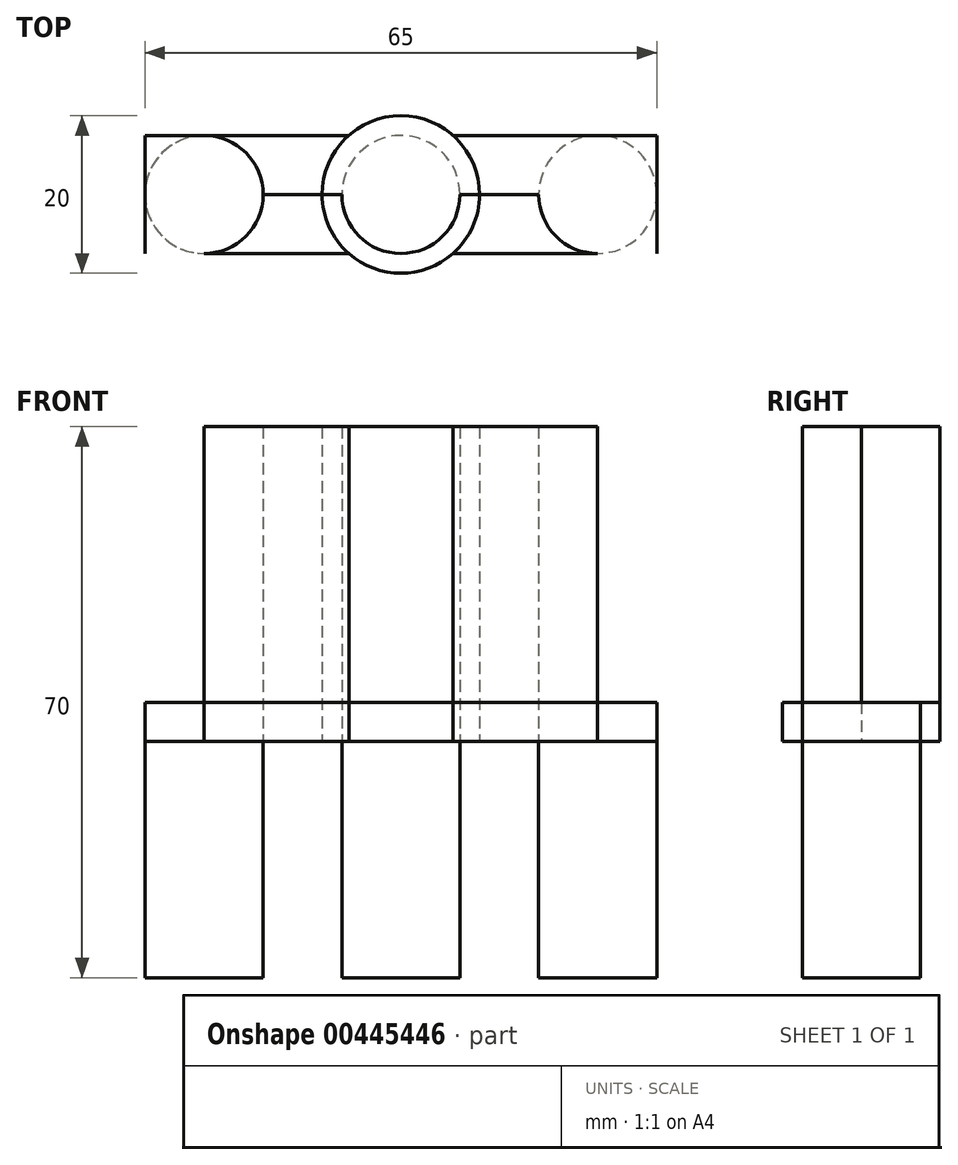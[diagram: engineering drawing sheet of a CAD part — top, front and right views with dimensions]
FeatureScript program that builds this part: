
annotation { "Feature Type Name" : "Feature", "Feature Type Description" : "" }
export const myFeature = defineFeature(function(context is Context, id is Id, definition is map)
    precondition{}
    {
        {
            var Q0;
            Q0=qCreatedBy(makeId("Top.planeOp"),FACE);
            var sketch = newSketch(context, id + "F0", { "sketchPlane" : qUnion([Q0])});
            skLineSegment(sketch, "E0.bottom", {"start": v(32.5, -7.5) * mm, "end": v(-32.5, -7.5) * mm});
            skLineSegment(sketch, "E0.top", {"start": v(32.5, 7.5) * mm, "end": v(-32.5, 7.5) * mm});
            skLineSegment(sketch, "E0.left", {"start": v(32.5, -7.5) * mm, "end": v(32.5, 7.5) * mm});
            skLineSegment(sketch, "E0.right", {"start": v(-32.5, -7.5) * mm, "end": v(-32.5, 7.5) * mm});
            skPoint(sketch, "E0.middle", {"position": v(0, 0) * mm});
            skCircle(sketch, "E1", {"center": v(0, 0) * mm, "radius": 10 * mm});
            skCircle(sketch, "E2", {"center": v(0, 0) * mm, "radius": 7.5 * mm});
            skLineSegment(sketch, "E3", {"start": v(0, 0) * mm, "end": v(25, 0) * mm});
            skLineSegment(sketch, "E4", {"start": v(0, 0) * mm, "end": v(-25, 0) * mm});
            skCircle(sketch, "E5", {"center": v(-25, 0) * mm, "radius": 7.5 * mm});
            skCircle(sketch, "E6", {"center": v(25, 0) * mm, "radius": 7.5 * mm});
            skSolve(sketch);
        }
        {
            var Q0;
            Q0 = qSketchRegion(id + "F0", true);
            var Q1;
            {var subQ0=sQuery(id+"F0.wireOp",EDGE,"E2");var subQ1=makeQuery(id+"F0.imprint","INTERSECT",VERTEX,{"derivedFrom":[sQuery(id+"F0.wireOp",EDGE,"E0.top"),subQ0]});Q1=makeQuery(id+"F0.imprint","IMPRINT",FACE,{"disambiguationData":[TD([[makeQuery(id+"F0.imprint","IMPRINT",EDGE,{"disambiguationData":[TD([[subQ1,1.0]])],"derivedFrom":subQ0}),1.0]])]});}
            var Q2;
            {var subQ0=sQuery(id+"F0.wireOp",EDGE,"E2");var subQ1=makeQuery(id+"F0.imprint","INTERSECT",VERTEX,{"derivedFrom":[sQuery(id+"F0.wireOp",EDGE,"E0.bottom"),subQ0]});Q2=makeQuery(id+"F0.imprint","IMPRINT",FACE,{"disambiguationData":[TD([[makeQuery(id+"F0.imprint","IMPRINT",EDGE,{"disambiguationData":[TD([[subQ1,1.0]])],"derivedFrom":subQ0}),1.0]])]});}
            extrude(context, id + "F1", {"entities" : qUnion([Q0, Q1, Q2]), "depth" : 5 * mm});
        }
        {
            var Q0;
            {var subQ0=sQuery(id+"F0.wireOp",EDGE,"E1");var subQ1=sQuery(id+"F0.wireOp",EDGE,"E0.top");var subQ2=makeQuery(id+"F0.imprint","INTERSECT",VERTEX,{"disambiguationData":[OD(0.0)],"derivedFrom":[subQ1,subQ0]});Q0=makeQuery(id+"F0.imprint","IMPRINT",FACE,{"disambiguationData":[TD([[makeQuery(id+"F0.imprint","IMPRINT",EDGE,{"disambiguationData":[TD([[subQ2,-1.0]])],"derivedFrom":subQ1}),-1.0]])]});}
            var Q1;
            {var subQ0=sQuery(id+"F0.wireOp",EDGE,"E1");var subQ1=sQuery(id+"F0.wireOp",EDGE,"E0.top");var subQ2=makeQuery(id+"F0.imprint","INTERSECT",VERTEX,{"disambiguationData":[OD(1.0)],"derivedFrom":[subQ1,subQ0]});Q1=makeQuery(id+"F0.imprint","IMPRINT",FACE,{"disambiguationData":[TD([[makeQuery(id+"F0.imprint","IMPRINT",EDGE,{"disambiguationData":[TD([[subQ2,1.0]])],"derivedFrom":subQ1}),1.0]])]});}
            var Q2;
            {var subQ0=sQuery(id+"F0.wireOp",EDGE,"E2");var subQ1=makeQuery(id+"F0.imprint","INTERSECT",VERTEX,{"derivedFrom":[sQuery(id+"F0.wireOp",EDGE,"E0.top"),subQ0]});Q2=makeQuery(id+"F0.imprint","IMPRINT",FACE,{"disambiguationData":[TD([[makeQuery(id+"F0.imprint","IMPRINT",EDGE,{"disambiguationData":[TD([[subQ1,1.0]])],"derivedFrom":subQ0}),1.0]])]});}
            var Q3;
            {var subQ0=sQuery(id+"F0.wireOp",EDGE,"E1");var subQ1=sQuery(id+"F0.wireOp",EDGE,"E0.top");var subQ2=makeQuery(id+"F0.imprint","INTERSECT",VERTEX,{"disambiguationData":[OD(0.0)],"derivedFrom":[subQ1,subQ0]});Q3=makeQuery(id+"F0.imprint","IMPRINT",FACE,{"disambiguationData":[TD([[makeQuery(id+"F0.imprint","IMPRINT",EDGE,{"disambiguationData":[TD([[subQ2,-1.0]])],"derivedFrom":subQ1}),1.0]])]});}
            var Q4;
            {var subQ0=sQuery(id+"F0.wireOp",EDGE,"E2");var subQ1=makeQuery(id+"F0.imprint","INTERSECT",VERTEX,{"derivedFrom":[sQuery(id+"F0.wireOp",EDGE,"E0.bottom"),subQ0]});Q4=makeQuery(id+"F0.imprint","IMPRINT",FACE,{"disambiguationData":[TD([[makeQuery(id+"F0.imprint","IMPRINT",EDGE,{"disambiguationData":[TD([[subQ1,1.0]])],"derivedFrom":subQ0}),1.0]])]});}
            var Q5;
            {var subQ0=sQuery(id+"F0.wireOp",EDGE,"E1");var subQ1=sQuery(id+"F0.wireOp",EDGE,"E0.bottom");var subQ2=makeQuery(id+"F0.imprint","INTERSECT",VERTEX,{"disambiguationData":[OD(0.0)],"derivedFrom":[subQ1,subQ0]});Q5=makeQuery(id+"F0.imprint","IMPRINT",FACE,{"disambiguationData":[TD([[makeQuery(id+"F0.imprint","IMPRINT",EDGE,{"disambiguationData":[TD([[subQ2,-1.0]])],"derivedFrom":subQ1}),1.0]])]});}
            var Q6;
            {var subQ0=sQuery(id+"F0.wireOp",EDGE,"E1");var subQ1=sQuery(id+"F0.wireOp",EDGE,"E0.bottom");var subQ2=makeQuery(id+"F0.imprint","INTERSECT",VERTEX,{"disambiguationData":[OD(0.0)],"derivedFrom":[subQ1,subQ0]});Q6=makeQuery(id+"F0.imprint","IMPRINT",FACE,{"disambiguationData":[TD([[makeQuery(id+"F0.imprint","IMPRINT",EDGE,{"disambiguationData":[TD([[subQ2,-1.0]])],"derivedFrom":subQ1}),-1.0]])]});}
            var Q7;
            {var subQ0=sQuery(id+"F0.wireOp",EDGE,"E1");var subQ1=sQuery(id+"F0.wireOp",EDGE,"E0.bottom");var subQ2=makeQuery(id+"F0.imprint","INTERSECT",VERTEX,{"disambiguationData":[OD(1.0)],"derivedFrom":[subQ1,subQ0]});Q7=makeQuery(id+"F0.imprint","IMPRINT",FACE,{"disambiguationData":[TD([[makeQuery(id+"F0.imprint","IMPRINT",EDGE,{"disambiguationData":[TD([[subQ2,1.0]])],"derivedFrom":subQ1}),-1.0]])]});}
            extrude(context, id + "F2", {"entities" : qUnion([Q0, Q1, Q2, Q3, Q4, Q5, Q6, Q7]), "depth" : 40 * mm});
        }
        {
            var Q0;
            {var subQ0=sQuery(id+"F0.wireOp",EDGE,"E5");var subQ1=makeQuery(id+"F0.imprint","INTERSECT",VERTEX,{"derivedFrom":[sQuery(id+"F0.wireOp",EDGE,"E0.top"),subQ0]});Q0=makeQuery(id+"F0.imprint","IMPRINT",FACE,{"disambiguationData":[TD([[makeQuery(id+"F0.imprint","IMPRINT",EDGE,{"disambiguationData":[TD([[subQ1,1.0]])],"derivedFrom":subQ0}),1.0]])]});}
            var Q1;
            {var subQ0=sQuery(id+"F0.wireOp",EDGE,"E2");var subQ1=makeQuery(id+"F0.imprint","INTERSECT",VERTEX,{"derivedFrom":[sQuery(id+"F0.wireOp",EDGE,"E0.top"),subQ0]});Q1=makeQuery(id+"F0.imprint","IMPRINT",FACE,{"disambiguationData":[TD([[makeQuery(id+"F0.imprint","IMPRINT",EDGE,{"disambiguationData":[TD([[subQ1,1.0]])],"derivedFrom":subQ0}),1.0]])]});}
            var Q2;
            {var subQ0=sQuery(id+"F0.wireOp",EDGE,"E2");var subQ1=makeQuery(id+"F0.imprint","INTERSECT",VERTEX,{"derivedFrom":[sQuery(id+"F0.wireOp",EDGE,"E0.bottom"),subQ0]});Q2=makeQuery(id+"F0.imprint","IMPRINT",FACE,{"disambiguationData":[TD([[makeQuery(id+"F0.imprint","IMPRINT",EDGE,{"disambiguationData":[TD([[subQ1,1.0]])],"derivedFrom":subQ0}),1.0]])]});}
            var Q3;
            {var subQ0=sQuery(id+"F0.wireOp",EDGE,"E6");var subQ1=makeQuery(id+"F0.imprint","INTERSECT",VERTEX,{"derivedFrom":[sQuery(id+"F0.wireOp",EDGE,"E0.top"),subQ0]});Q3=makeQuery(id+"F0.imprint","IMPRINT",FACE,{"disambiguationData":[TD([[makeQuery(id+"F0.imprint","IMPRINT",EDGE,{"disambiguationData":[TD([[subQ1,1.0]])],"derivedFrom":subQ0}),1.0]])]});}
            extrude(context, id + "F3", {"entities" : qUnion([Q0, Q1, Q2, Q3]), "oppositeDirection" : true, "depth" : 30 * mm});
        }
    });
